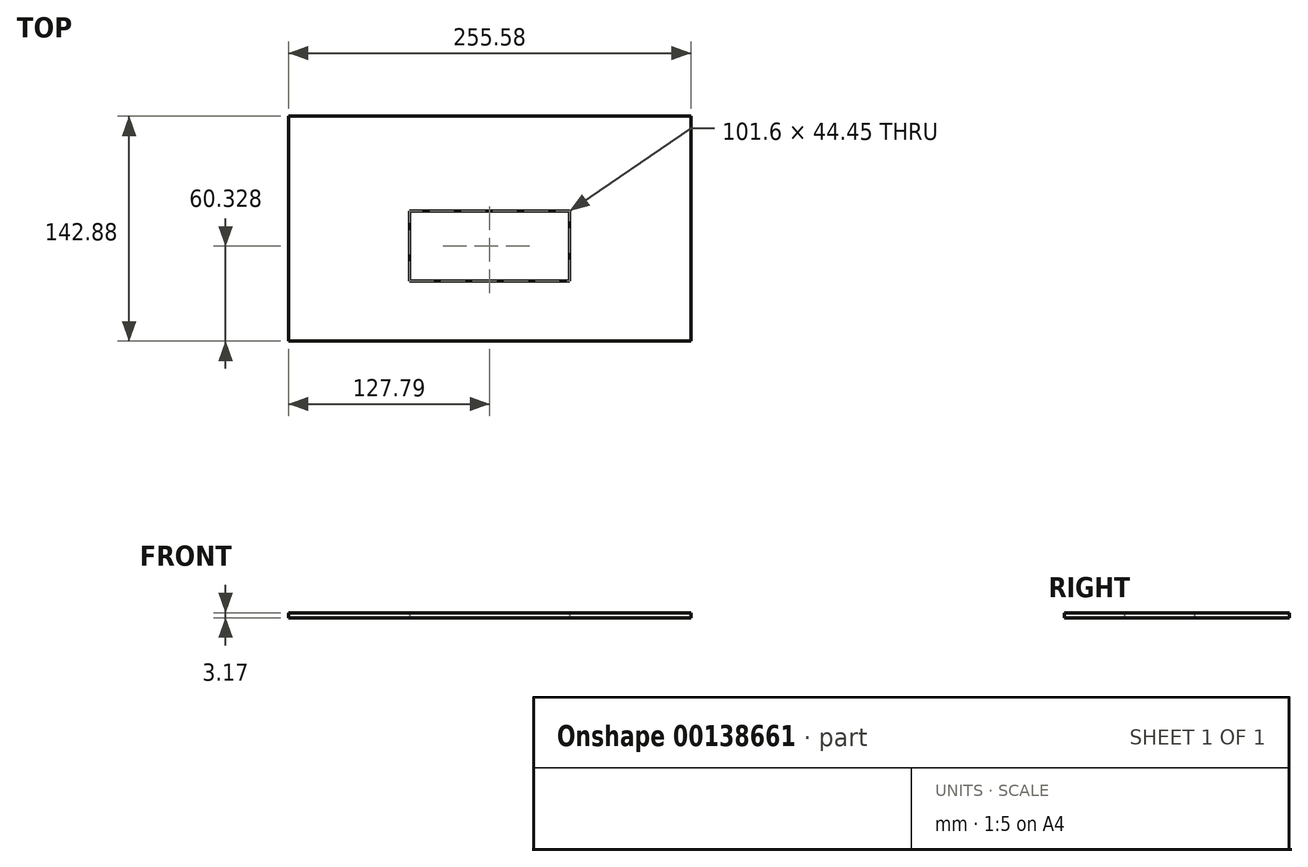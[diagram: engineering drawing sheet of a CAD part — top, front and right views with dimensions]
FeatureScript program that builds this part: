
annotation { "Feature Type Name" : "Feature", "Feature Type Description" : "" }
export const myFeature = defineFeature(function(context is Context, id is Id, definition is map)
    precondition{}
    {
        {
            var Q0;
            Q0=qCreatedBy(makeId("Top.planeOp"),FACE);
            var sketch = newSketch(context, id + "F0", { "sketchPlane" : qUnion([Q0])});
            skLineSegment(sketch, "E0.bottom", {"start": v(127.8, -71.44) * mm, "end": v(-127.8, -71.44) * mm});
            skLineSegment(sketch, "E0.top", {"start": v(127.8, 71.44) * mm, "end": v(-127.8, 71.44) * mm});
            skLineSegment(sketch, "E0.left", {"start": v(127.8, -71.44) * mm, "end": v(127.8, 71.44) * mm});
            skLineSegment(sketch, "E0.right", {"start": v(-127.8, -71.44) * mm, "end": v(-127.8, 71.44) * mm});
            skPoint(sketch, "E0.middle", {"position": v(0, 0) * mm});
            skLineSegment(sketch, "E1.bottom", {"start": v(50.8, -33.34) * mm, "end": v(-50.8, -33.34) * mm});
            skLineSegment(sketch, "E1.top", {"start": v(50.8, 11.11) * mm, "end": v(-50.8, 11.11) * mm});
            skLineSegment(sketch, "E1.left", {"start": v(50.8, -33.34) * mm, "end": v(50.8, 11.11) * mm});
            skLineSegment(sketch, "E1.right", {"start": v(-50.8, -33.34) * mm, "end": v(-50.8, 11.11) * mm});
            skPoint(sketch, "E1.middle", {"position": v(0, -11.11) * mm});
            skSolve(sketch);
        }
        {
            var Q0;
            Q0=makeQuery(id+"F0.imprint","IMPRINT",FACE,{"disambiguationData":[TD([[makeQuery(id+"F0.imprint","IMPRINT",EDGE,{"derivedFrom":sQuery(id+"F0.wireOp",EDGE,"E0.bottom")}),-1.0]])]});
            extrude(context, id + "F1", {"entities" : qUnion([Q0]), "depth" : 3.17 * mm});
        }
    });
